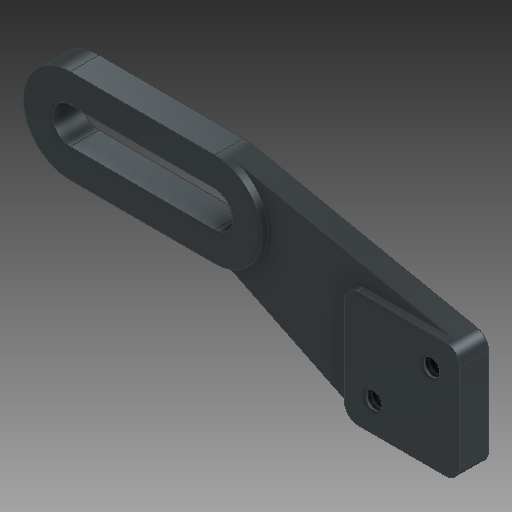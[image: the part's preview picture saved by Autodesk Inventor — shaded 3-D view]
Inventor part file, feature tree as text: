
AUTODESK INVENTOR PART (.ipt)
format: ipt  version: 2020 (Build 240168000, 168)  size: 210,432 bytes
history: native  units: in
note: dims shown in document units (in); Inventor stores cm internally (conversion verified against a paired STEP export)
features: sketch x5, extrude x4, projected_geometry x3, hole x1
ambient origin geometry x8: Origin, YZ Plane, XZ Plane, XY Plane, X Axis, Y Axis, Z Axis, Center Point
bodies: Solid1 (feature_tree)
feature tree (13):
  extrude  "Extrusion1"  Depth=0.125in
  extrude  "Extrusion2"  Depth=0.4062in
  extrude  "Extrusion3"  Depth=0.5in
  extrude  "Extrusion4"  Depth=0.125in
  hole  "Hole1"  [1 undecoded]
  sketch  "Sketch1"  dims[d0=0.125in d1=2.0in]
  sketch  "Sketch2"  dims[d2=1.25in d4=0.4062in]
  projected_geometry  "Projected Loop1"
  sketch  "Sketch3"  dims[d5=0.5in d6=0.75in]
  projected_geometry  "Projected Loop2"
  sketch  "Sketch4"  dims[d7=0.125in d8=0.75in]
  projected_geometry  "Projected Loop3"
  sketch  "Sketch5"  dims[d9=0.5127in d10=0.125in d11=1.0583in d12=0.1875in d13=0.0in d14=1.25in d15=0.0625in d16=0.0in d17=1.0in d18=1.0in d19=0.125in d20=0.25in d21=0.0in d22=0.3125in d23=0.25in d24=0.0in d25=0.75in d26=0.25in d27=0.5in d28=0.25in d29=0.145in d30=0.38in d31=0.4062in d32=0.25in d33=0.5635in d34=0.588in d35=0.8108in]
note: 1 required parameter value undecoded (feature->parameter linkage not recoverable at this tier; creation-order binding heuristic only, values carry confidence <= 0.55)
